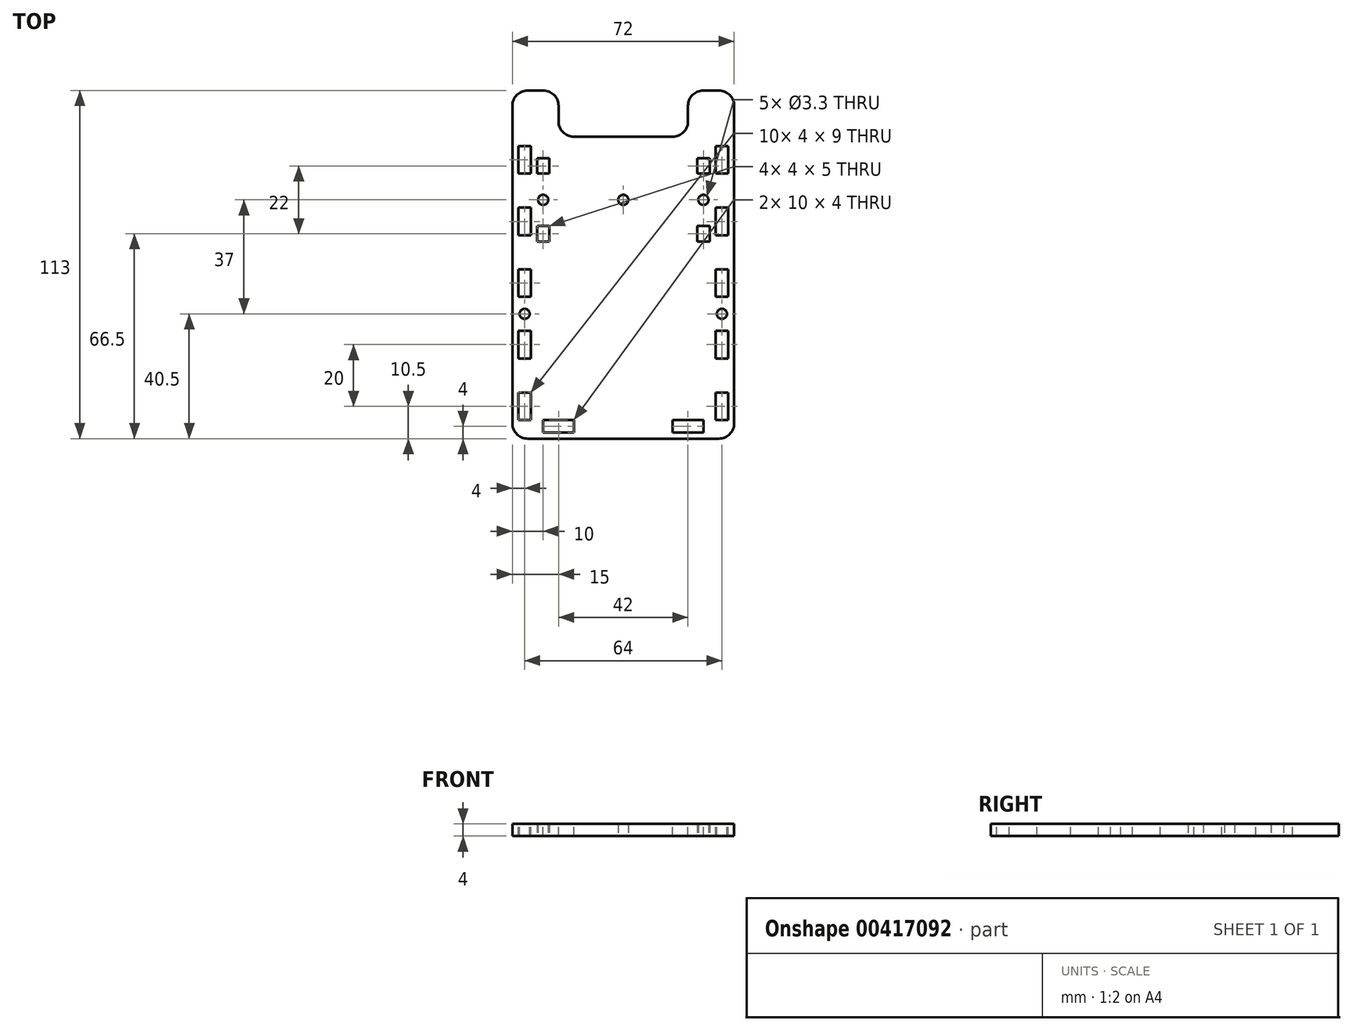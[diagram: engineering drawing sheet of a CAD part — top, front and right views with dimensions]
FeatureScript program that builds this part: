
annotation { "Feature Type Name" : "Feature", "Feature Type Description" : "" }
export const myFeature = defineFeature(function(context is Context, id is Id, definition is map)
    precondition{}
    {
        {
            var Q0;
            Q0=qCreatedBy(makeId("Top.planeOp"),FACE);
            var sketch = newSketch(context, id + "F0", { "sketchPlane" : qUnion([Q0])});
            skLineSegment(sketch, "E0.bottom", {"start": v(30, -17.5) * mm, "end": v(18.9, -17.5) * mm});
            skLineSegment(sketch, "E0.top", {"start": v(30, 17.5) * mm, "end": v(-30, 17.5) * mm});
            skLineSegment(sketch, "E0.left", {"start": v(30, -17.5) * mm, "end": v(30, 17.5) * mm});
            skLineSegment(sketch, "E0.right", {"start": v(-30, -17.5) * mm, "end": v(-30, 17.5) * mm});
            skPoint(sketch, "E0.middle", {"position": v(0, 0) * mm});
            skLineSegment(sketch, "E1.bottom", {"start": v(-24, 8.5) * mm, "end": v(-28, 8.5) * mm});
            skLineSegment(sketch, "E1.top", {"start": v(-24, 13.5) * mm, "end": v(-28, 13.5) * mm});
            skLineSegment(sketch, "E1.left", {"start": v(-24, 8.5) * mm, "end": v(-24, 13.5) * mm});
            skLineSegment(sketch, "E1.right", {"start": v(-28, 8.5) * mm, "end": v(-28, 13.5) * mm});
            skPoint(sketch, "E1.middle", {"position": v(-26, 11) * mm});
            skLineSegment(sketch, "E2.MirrorCS", {"start": v(-28, -8.5) * mm, "end": v(-28, -13.5) * mm});
            skLineSegment(sketch, "E3.MirrorCS", {"start": v(-24, -8.5) * mm, "end": v(-24, -13.5) * mm});
            skLineSegment(sketch, "E4.MirrorCS", {"start": v(-24, -8.5) * mm, "end": v(-28, -8.5) * mm});
            skLineSegment(sketch, "E5.MirrorCS", {"start": v(-24, -13.5) * mm, "end": v(-28, -13.5) * mm});
            skPoint(sketch, "E6.MirrorP", {"position": v(-26, -11) * mm});
            skPoint(sketch, "E7.MirrorP", {"position": v(26, 11) * mm});
            skPoint(sketch, "E8.MirrorP", {"position": v(26, -11) * mm});
            skLineSegment(sketch, "E9.MirrorCS", {"start": v(24, -13.5) * mm, "end": v(28, -13.5) * mm});
            skLineSegment(sketch, "E10.MirrorCS", {"start": v(24, -8.5) * mm, "end": v(28, -8.5) * mm});
            skLineSegment(sketch, "E11.MirrorCS", {"start": v(24, -8.5) * mm, "end": v(24, -13.5) * mm});
            skLineSegment(sketch, "E12.MirrorCS", {"start": v(24, 8.5) * mm, "end": v(28, 8.5) * mm});
            skLineSegment(sketch, "E13.MirrorCS", {"start": v(28, -8.5) * mm, "end": v(28, -13.5) * mm});
            skLineSegment(sketch, "E14.MirrorCS", {"start": v(28, 8.5) * mm, "end": v(28, 13.5) * mm});
            skLineSegment(sketch, "E15.MirrorCS", {"start": v(24, 8.5) * mm, "end": v(24, 13.5) * mm});
            skLineSegment(sketch, "E16.MirrorCS", {"start": v(24, 13.5) * mm, "end": v(28, 13.5) * mm});
            skPoint(sketch, "E17", {"position": v(-26, 0) * mm});
            skPoint(sketch, "E18.MirrorP", {"position": v(26, 0) * mm});
            skLineSegment(sketch, "E19", {"start": v(-18.9, -17.5) * mm, "end": v(-20, -14.5) * mm});
            skLineSegment(sketch, "E20", {"start": v(-20, -14.5) * mm, "end": v(-5, -14.5) * mm, "construction": true});
            skLineSegment(sketch, "E21", {"start": v(-5, -14.5) * mm, "end": v(-6.1, -17.5) * mm});
            skLineSegment(sketch, "E22.trimOffspring", {"start": v(-18.9, -17.5) * mm, "end": v(-30, -17.5) * mm});
            skLineSegment(sketch, "E23.MirrorCS", {"start": v(5, -14.5) * mm, "end": v(6.1, -17.5) * mm});
            skLineSegment(sketch, "E24.MirrorCS", {"start": v(18.9, -17.5) * mm, "end": v(20, -14.5) * mm});
            skLineSegment(sketch, "E25.MirrorCS", {"start": v(20, -14.5) * mm, "end": v(5, -14.5) * mm, "construction": true});
            skLineSegment(sketch, "E26.trimOffspring", {"start": v(6.1, -17.5) * mm, "end": v(-6.1, -17.5) * mm});
            skLineSegment(sketch, "E27", {"start": v(-18.9, -17.5) * mm, "end": v(-6.1, -17.5) * mm});
            skLineSegment(sketch, "E28", {"start": v(6.1, -17.5) * mm, "end": v(18.9, -17.5) * mm});
            skSolve(sketch);
        }
        {
            var Q0;
            Q0=makeQuery(id+"F0.imprint","IMPRINT",FACE,{"disambiguationData":[TD([[makeQuery(id+"F0.imprint","IMPRINT",EDGE,{"derivedFrom":sQuery(id+"F0.wireOp",EDGE,"E0.bottom")}),-1.0]])]});
            extrude(context, id + "F1", {"entities" : qUnion([Q0]), "depth" : 4 * mm});
        }
        {
            var Q0;
            Q0=sQuery(id+"F0.wireOp",VERTEX,"E17");
            var Q1;
            Q1=sQuery(id+"F0.wireOp",VERTEX,"E18.MirrorP");
            var Q2;
            Q2=makeQuery(id+"F1.opExtrude","SWEPT_BODY",BODY,{"disambiguationData":[OSD([sQuery(id+"F0.wireOp",EDGE,"E0.bottom"),sQuery(id+"F0.wireOp",EDGE,"E0.top"),sQuery(id+"F0.wireOp",EDGE,"E0.left"),sQuery(id+"F0.wireOp",EDGE,"E0.right"),sQuery(id+"F0.wireOp",EDGE,"E1.bottom"),sQuery(id+"F0.wireOp",EDGE,"E1.top"),sQuery(id+"F0.wireOp",EDGE,"E1.left"),sQuery(id+"F0.wireOp",EDGE,"E1.right"),sQuery(id+"F0.wireOp",EDGE,"E2.MirrorCS"),sQuery(id+"F0.wireOp",EDGE,"E3.MirrorCS"),sQuery(id+"F0.wireOp",EDGE,"E4.MirrorCS"),sQuery(id+"F0.wireOp",EDGE,"E5.MirrorCS"),sQuery(id+"F0.wireOp",EDGE,"E9.MirrorCS"),sQuery(id+"F0.wireOp",EDGE,"E10.MirrorCS"),sQuery(id+"F0.wireOp",EDGE,"E11.MirrorCS"),sQuery(id+"F0.wireOp",EDGE,"E12.MirrorCS"),sQuery(id+"F0.wireOp",EDGE,"E13.MirrorCS"),sQuery(id+"F0.wireOp",EDGE,"E14.MirrorCS"),sQuery(id+"F0.wireOp",EDGE,"E15.MirrorCS"),sQuery(id+"F0.wireOp",EDGE,"E16.MirrorCS"),sQuery(id+"F0.wireOp",EDGE,"sCp7zdMq-uB77-Oyxq-tNPJ-BeyvnlYmejad.bottom"),sQuery(id+"F0.wireOp",EDGE,"sCp7zdMq-uB77-Oyxq-tNPJ-BeyvnlYmejad.top"),sQuery(id+"F0.wireOp",EDGE,"sCp7zdMq-uB77-Oyxq-tNPJ-BeyvnlYmejad.left"),sQuery(id+"F0.wireOp",EDGE,"sCp7zdMq-uB77-Oyxq-tNPJ-BeyvnlYmejad.right")])]});
            hole(context, id + "F2", {"style" : HoleStyle.SIMPLE, "endStyle" : HoleEndStyle.THROUGH, "oppositeDirection" : true, "standardTappedOrClearance" : lookupTablePath({ "standard" : "ISO", "fit" : "Normal", "size" : "M3", "type" : "Clearance" }), "standardBlindInLast" : lookupTablePath({ "fit" : "Standard", "standard" : "ISO", "size" : "M3", "type" : "Clearance" }), "holeDiameter" : 3.3 * mm, "isTappedThrough" : true, "tappedDepth" : 12 * mm, "tapClearance" : 3, "startFromSketch" : true, "locations" : qUnion([Q0, Q1]), "scope" : qUnion([Q2])});
        }
        {
            var Q0;
            Q0=sQuery(id+"F0.wireOp",VERTEX,"E0.middle");
            var Q1;
            Q1=makeQuery(id+"F1.opExtrude","SWEPT_BODY",BODY,{"disambiguationData":[OSD([sQuery(id+"F0.wireOp",EDGE,"E0.bottom"),sQuery(id+"F0.wireOp",EDGE,"E0.top"),sQuery(id+"F0.wireOp",EDGE,"E0.left"),sQuery(id+"F0.wireOp",EDGE,"E0.right"),sQuery(id+"F0.wireOp",EDGE,"E1.bottom"),sQuery(id+"F0.wireOp",EDGE,"E1.top"),sQuery(id+"F0.wireOp",EDGE,"E1.left"),sQuery(id+"F0.wireOp",EDGE,"E1.right"),sQuery(id+"F0.wireOp",EDGE,"E2.MirrorCS"),sQuery(id+"F0.wireOp",EDGE,"E3.MirrorCS"),sQuery(id+"F0.wireOp",EDGE,"E4.MirrorCS"),sQuery(id+"F0.wireOp",EDGE,"E5.MirrorCS"),sQuery(id+"F0.wireOp",EDGE,"E9.MirrorCS"),sQuery(id+"F0.wireOp",EDGE,"E10.MirrorCS"),sQuery(id+"F0.wireOp",EDGE,"E11.MirrorCS"),sQuery(id+"F0.wireOp",EDGE,"E12.MirrorCS"),sQuery(id+"F0.wireOp",EDGE,"E13.MirrorCS"),sQuery(id+"F0.wireOp",EDGE,"E14.MirrorCS"),sQuery(id+"F0.wireOp",EDGE,"E15.MirrorCS"),sQuery(id+"F0.wireOp",EDGE,"E16.MirrorCS"),sQuery(id+"F0.wireOp",EDGE,"E19"),sQuery(id+"F0.wireOp",EDGE,"E20"),sQuery(id+"F0.wireOp",EDGE,"E21"),sQuery(id+"F0.wireOp",EDGE,"E22.trimOffspring"),sQuery(id+"F0.wireOp",EDGE,"E23.MirrorCS"),sQuery(id+"F0.wireOp",EDGE,"E24.MirrorCS"),sQuery(id+"F0.wireOp",EDGE,"E25.MirrorCS"),sQuery(id+"F0.wireOp",EDGE,"E26.trimOffspring")])]});
            hole(context, id + "F3", {"style" : HoleStyle.SIMPLE, "endStyle" : HoleEndStyle.THROUGH, "oppositeDirection" : true, "standardTappedOrClearance" : lookupTablePath({ "standard" : "ISO", "fit" : "Normal", "size" : "M3", "type" : "Clearance" }), "standardBlindInLast" : lookupTablePath({ "fit" : "Standard", "standard" : "ISO", "size" : "M3", "type" : "Clearance" }), "holeDiameter" : 3.3 * mm, "isTappedThrough" : true, "tappedDepth" : 12 * mm, "tapClearance" : 3, "startFromSketch" : true, "locations" : qUnion([Q0]), "scope" : qUnion([Q1])});
        }
        {
            var Q0;
            Q0=makeQuery(id+"F1.opExtrude","CAP_FACE",FACE,{"disambiguationData":[OSD([sQuery(id+"F0.wireOp",EDGE,"E0.bottom"),sQuery(id+"F0.wireOp",EDGE,"E0.top"),sQuery(id+"F0.wireOp",EDGE,"E0.left"),sQuery(id+"F0.wireOp",EDGE,"E0.right"),sQuery(id+"F0.wireOp",EDGE,"E1.bottom"),sQuery(id+"F0.wireOp",EDGE,"E1.top"),sQuery(id+"F0.wireOp",EDGE,"E1.left"),sQuery(id+"F0.wireOp",EDGE,"E1.right"),sQuery(id+"F0.wireOp",EDGE,"E2.MirrorCS"),sQuery(id+"F0.wireOp",EDGE,"E3.MirrorCS"),sQuery(id+"F0.wireOp",EDGE,"E4.MirrorCS"),sQuery(id+"F0.wireOp",EDGE,"E5.MirrorCS"),sQuery(id+"F0.wireOp",EDGE,"E9.MirrorCS"),sQuery(id+"F0.wireOp",EDGE,"E10.MirrorCS"),sQuery(id+"F0.wireOp",EDGE,"E11.MirrorCS"),sQuery(id+"F0.wireOp",EDGE,"E12.MirrorCS"),sQuery(id+"F0.wireOp",EDGE,"E13.MirrorCS"),sQuery(id+"F0.wireOp",EDGE,"E14.MirrorCS"),sQuery(id+"F0.wireOp",EDGE,"E15.MirrorCS"),sQuery(id+"F0.wireOp",EDGE,"E16.MirrorCS"),sQuery(id+"F0.wireOp",EDGE,"E22.trimOffspring"),sQuery(id+"F0.wireOp",EDGE,"E26.trimOffspring"),sQuery(id+"F0.wireOp",EDGE,"E27"),sQuery(id+"F0.wireOp",EDGE,"E28")])],"isStart":false});
            var sketch = newSketch(context, id + "F4", { "sketchPlane" : qUnion([Q0])});
            skLineSegment(sketch, "E29.bottom", {"start": v(36, 17.5) * mm, "end": v(-36, 17.5) * mm, "construction": true});
            skLineSegment(sketch, "E29.top", {"start": v(36, -77.5) * mm, "end": v(-36, -77.5) * mm});
            skLineSegment(sketch, "E29.left", {"start": v(36, 17.5) * mm, "end": v(36, -77.5) * mm});
            skLineSegment(sketch, "E29.right", {"start": v(-36, 17.5) * mm, "end": v(-36, -77.5) * mm});
            skPoint(sketch, "E29.middle", {"position": v(0, -30) * mm});
            skLineSegment(sketch, "E30", {"start": v(-36, 17.5) * mm, "end": v(-36, 35.5) * mm});
            skLineSegment(sketch, "E31", {"start": v(-36, 35.5) * mm, "end": v(-21, 35.5) * mm});
            skLineSegment(sketch, "E32", {"start": v(-21, 35.5) * mm, "end": v(-21, 20.5) * mm});
            skLineSegment(sketch, "E33", {"start": v(-21, 20.5) * mm, "end": v(0, 20.5) * mm});
            skLineSegment(sketch, "E34.MirrorCS", {"start": v(21, 20.5) * mm, "end": v(0, 20.5) * mm});
            skLineSegment(sketch, "E35.MirrorCS", {"start": v(21, 35.5) * mm, "end": v(21, 20.5) * mm});
            skLineSegment(sketch, "E36.MirrorCS", {"start": v(36, 35.5) * mm, "end": v(21, 35.5) * mm});
            skLineSegment(sketch, "E37.MirrorCS", {"start": v(36, 17.5) * mm, "end": v(36, 35.5) * mm});
            skLineSegment(sketch, "E38.bottom", {"start": v(-30, 17.5) * mm, "end": v(-34, 17.5) * mm});
            skLineSegment(sketch, "E38.top", {"start": v(-30, 8.5) * mm, "end": v(-34, 8.5) * mm});
            skLineSegment(sketch, "E38.left", {"start": v(-30, 17.5) * mm, "end": v(-30, 8.5) * mm});
            skLineSegment(sketch, "E38.right", {"start": v(-34, 17.5) * mm, "end": v(-34, 8.5) * mm});
            skLineSegment(sketch, "E39.0.1.0", {"start": v(-34, -2.5) * mm, "end": v(-34, -11.5) * mm});
            skLineSegment(sketch, "E39.0.1.1", {"start": v(-30, -11.5) * mm, "end": v(-34, -11.5) * mm});
            skLineSegment(sketch, "E39.0.1.2", {"start": v(-30, -2.5) * mm, "end": v(-30, -11.5) * mm});
            skLineSegment(sketch, "E39.0.1.3", {"start": v(-30, -2.5) * mm, "end": v(-34, -2.5) * mm});
            skLineSegment(sketch, "E39.0.2.0", {"start": v(-34, -22.5) * mm, "end": v(-34, -31.5) * mm});
            skLineSegment(sketch, "E39.0.2.1", {"start": v(-30, -31.5) * mm, "end": v(-34, -31.5) * mm});
            skLineSegment(sketch, "E39.0.2.2", {"start": v(-30, -22.5) * mm, "end": v(-30, -31.5) * mm});
            skLineSegment(sketch, "E39.0.2.3", {"start": v(-30, -22.5) * mm, "end": v(-34, -22.5) * mm});
            skLineSegment(sketch, "E39.0.3.0", {"start": v(-34, -42.5) * mm, "end": v(-34, -51.5) * mm});
            skLineSegment(sketch, "E39.0.3.1", {"start": v(-30, -51.5) * mm, "end": v(-34, -51.5) * mm});
            skLineSegment(sketch, "E39.0.3.2", {"start": v(-30, -42.5) * mm, "end": v(-30, -51.5) * mm});
            skLineSegment(sketch, "E39.0.3.3", {"start": v(-30, -42.5) * mm, "end": v(-34, -42.5) * mm});
            skLineSegment(sketch, "E39.0.4.0", {"start": v(-34, -62.5) * mm, "end": v(-34, -71.5) * mm});
            skLineSegment(sketch, "E39.0.4.1", {"start": v(-30, -71.5) * mm, "end": v(-34, -71.5) * mm});
            skLineSegment(sketch, "E39.0.4.2", {"start": v(-30, -62.5) * mm, "end": v(-30, -71.5) * mm});
            skLineSegment(sketch, "E39.0.4.3", {"start": v(-30, -62.5) * mm, "end": v(-34, -62.5) * mm});
            skLineSegment(sketch, "E39.direction1", {"start": v(-34, 8.5) * mm, "end": v(-8, 8.5) * mm, "construction": true});
            skLineSegment(sketch, "E39.direction2", {"start": v(-34, 8.5) * mm, "end": v(-34, -11.5) * mm, "construction": true});
            skLineSegment(sketch, "E40.MirrorCS", {"start": v(34, -2.5) * mm, "end": v(34, -11.5) * mm});
            skLineSegment(sketch, "E41.MirrorCS", {"start": v(30, 17.5) * mm, "end": v(34, 17.5) * mm});
            skLineSegment(sketch, "E42.MirrorCS", {"start": v(30, 8.5) * mm, "end": v(34, 8.5) * mm});
            skLineSegment(sketch, "E43.MirrorCS", {"start": v(30, -42.5) * mm, "end": v(30, -51.5) * mm});
            skLineSegment(sketch, "E44.MirrorCS", {"start": v(30, -2.5) * mm, "end": v(34, -2.5) * mm});
            skLineSegment(sketch, "E45.MirrorCS", {"start": v(30, -51.5) * mm, "end": v(34, -51.5) * mm});
            skLineSegment(sketch, "E46.MirrorCS", {"start": v(30, -2.5) * mm, "end": v(30, -11.5) * mm});
            skLineSegment(sketch, "E47.MirrorCS", {"start": v(34, -42.5) * mm, "end": v(34, -51.5) * mm});
            skLineSegment(sketch, "E48.MirrorCS", {"start": v(30, -11.5) * mm, "end": v(34, -11.5) * mm});
            skLineSegment(sketch, "E49.MirrorCS", {"start": v(34, 8.5) * mm, "end": v(34, -11.5) * mm, "construction": true});
            skLineSegment(sketch, "E50.MirrorCS", {"start": v(30, -22.5) * mm, "end": v(34, -22.5) * mm});
            skLineSegment(sketch, "E51.MirrorCS", {"start": v(34, 8.5) * mm, "end": v(8, 8.5) * mm, "construction": true});
            skLineSegment(sketch, "E52.MirrorCS", {"start": v(-36, 17.5) * mm, "end": v(36, 17.5) * mm, "construction": true});
            skLineSegment(sketch, "E53.MirrorCS", {"start": v(30, -31.5) * mm, "end": v(34, -31.5) * mm});
            skLineSegment(sketch, "E54.MirrorCS", {"start": v(30, 17.5) * mm, "end": v(30, 8.5) * mm});
            skLineSegment(sketch, "E55.MirrorCS", {"start": v(30, -62.5) * mm, "end": v(30, -71.5) * mm});
            skLineSegment(sketch, "E56.MirrorCS", {"start": v(30, -62.5) * mm, "end": v(34, -62.5) * mm});
            skLineSegment(sketch, "E57.MirrorCS", {"start": v(34, 17.5) * mm, "end": v(34, 8.5) * mm});
            skLineSegment(sketch, "E58.MirrorCS", {"start": v(30, -42.5) * mm, "end": v(34, -42.5) * mm});
            skLineSegment(sketch, "E59.MirrorCS", {"start": v(30, -71.5) * mm, "end": v(34, -71.5) * mm});
            skLineSegment(sketch, "E60.MirrorCS", {"start": v(30, -22.5) * mm, "end": v(30, -31.5) * mm});
            skLineSegment(sketch, "E61.MirrorCS", {"start": v(34, -22.5) * mm, "end": v(34, -31.5) * mm});
            skLineSegment(sketch, "E62.MirrorCS", {"start": v(34, -62.5) * mm, "end": v(34, -71.5) * mm});
            skLineSegment(sketch, "E63.bottom", {"start": v(-26, -71.5) * mm, "end": v(-16, -71.5) * mm});
            skLineSegment(sketch, "E63.top", {"start": v(-26, -75.5) * mm, "end": v(-16, -75.5) * mm});
            skLineSegment(sketch, "E63.left", {"start": v(-26, -71.5) * mm, "end": v(-26, -75.5) * mm});
            skLineSegment(sketch, "E63.right", {"start": v(-16, -71.5) * mm, "end": v(-16, -75.5) * mm});
            skLineSegment(sketch, "E64.MirrorCS", {"start": v(26, -75.5) * mm, "end": v(16, -75.5) * mm});
            skLineSegment(sketch, "E65.MirrorCS", {"start": v(26, -71.5) * mm, "end": v(26, -75.5) * mm});
            skLineSegment(sketch, "E66.MirrorCS", {"start": v(16, -71.5) * mm, "end": v(16, -75.5) * mm});
            skLineSegment(sketch, "E67.MirrorCS", {"start": v(26, -71.5) * mm, "end": v(16, -71.5) * mm});
            skLineSegment(sketch, "E68", {"start": v(-32, -31.5) * mm, "end": v(-32, -42.5) * mm, "construction": true});
            skPoint(sketch, "E69", {"position": v(-32, -37) * mm});
            skLineSegment(sketch, "E70", {"start": v(32, -31.5) * mm, "end": v(32, -42.5) * mm, "construction": true});
            skPoint(sketch, "E71", {"position": v(32, -37) * mm});
            skSolve(sketch);
        }
        {
            var Q0;
            Q0=makeQuery(id+"F4.imprint","IMPRINT",FACE,{"disambiguationData":[TD([[makeQuery(id+"F4.imprint","IMPRINT",EDGE,{"derivedFrom":sQuery(id+"F4.wireOp",EDGE,"E29.top")}),-1.0]])]});
            extrude(context, id + "F5", {"entities" : qUnion([Q0]), "operationType" : NewBodyOperationType.ADD, "oppositeDirection" : true, "depth" : 4 * mm});
        }
        {
            var Q0;
            Q0=sQuery(id+"F4.wireOp",VERTEX,"E69");
            var Q1;
            Q1=sQuery(id+"F4.wireOp",VERTEX,"E71");
            var Q2;
            Q2=makeQuery(id+"F1.opExtrude","SWEPT_BODY",BODY,{"disambiguationData":[OSD([sQuery(id+"F0.wireOp",EDGE,"E0.bottom"),sQuery(id+"F0.wireOp",EDGE,"E0.top"),sQuery(id+"F0.wireOp",EDGE,"E0.left"),sQuery(id+"F0.wireOp",EDGE,"E0.right"),sQuery(id+"F0.wireOp",EDGE,"E1.bottom"),sQuery(id+"F0.wireOp",EDGE,"E1.top"),sQuery(id+"F0.wireOp",EDGE,"E1.left"),sQuery(id+"F0.wireOp",EDGE,"E1.right"),sQuery(id+"F0.wireOp",EDGE,"E2.MirrorCS"),sQuery(id+"F0.wireOp",EDGE,"E3.MirrorCS"),sQuery(id+"F0.wireOp",EDGE,"E4.MirrorCS"),sQuery(id+"F0.wireOp",EDGE,"E5.MirrorCS"),sQuery(id+"F0.wireOp",EDGE,"E9.MirrorCS"),sQuery(id+"F0.wireOp",EDGE,"E10.MirrorCS"),sQuery(id+"F0.wireOp",EDGE,"E11.MirrorCS"),sQuery(id+"F0.wireOp",EDGE,"E12.MirrorCS"),sQuery(id+"F0.wireOp",EDGE,"E13.MirrorCS"),sQuery(id+"F0.wireOp",EDGE,"E14.MirrorCS"),sQuery(id+"F0.wireOp",EDGE,"E15.MirrorCS"),sQuery(id+"F0.wireOp",EDGE,"E16.MirrorCS"),sQuery(id+"F0.wireOp",EDGE,"E22.trimOffspring"),sQuery(id+"F0.wireOp",EDGE,"E26.trimOffspring"),sQuery(id+"F0.wireOp",EDGE,"E27"),sQuery(id+"F0.wireOp",EDGE,"E28")])]});
            hole(context, id + "F6", {"style" : HoleStyle.SIMPLE, "endStyle" : HoleEndStyle.THROUGH, "standardTappedOrClearance" : lookupTablePath({ "standard" : "ISO", "fit" : "Normal", "size" : "M3", "type" : "Clearance" }), "standardBlindInLast" : lookupTablePath({ "fit" : "Standard", "standard" : "ISO", "size" : "M3", "type" : "Clearance" }), "holeDiameter" : 3.3 * mm, "isTappedThrough" : true, "tappedDepth" : 12 * mm, "tapClearance" : 3, "startFromSketch" : true, "locations" : qUnion([Q0, Q1]), "scope" : qUnion([Q2])});
        }
        {
            var Q0;
            Q0=makeQuery(id+"F5.opExtrude","SWEPT_EDGE",EDGE,{"disambiguationData":[OSD([sQuery(id+"F4.wireOp",EDGE,"E29.top"),sQuery(id+"F4.wireOp",EDGE,"E29.right")])]});
            var Q1;
            Q1=makeQuery(id+"F5.opExtrude","SWEPT_EDGE",EDGE,{"disambiguationData":[OSD([sQuery(id+"F4.wireOp",EDGE,"E29.top"),sQuery(id+"F4.wireOp",EDGE,"E29.left")])]});
            var Q2;
            Q2=makeQuery(id+"F5.opExtrude","SWEPT_EDGE",EDGE,{"disambiguationData":[OSD([sQuery(id+"F4.wireOp",EDGE,"E32"),sQuery(id+"F4.wireOp",EDGE,"E33")])]});
            var Q3;
            Q3=makeQuery(id+"F5.opExtrude","SWEPT_EDGE",EDGE,{"disambiguationData":[OSD([sQuery(id+"F4.wireOp",EDGE,"E31"),sQuery(id+"F4.wireOp",EDGE,"E32")])]});
            var Q4;
            Q4=makeQuery(id+"F5.opExtrude","SWEPT_EDGE",EDGE,{"disambiguationData":[OSD([sQuery(id+"F4.wireOp",EDGE,"E30"),sQuery(id+"F4.wireOp",EDGE,"E31")])]});
            var Q5;
            Q5=makeQuery(id+"F5.opExtrude","SWEPT_EDGE",EDGE,{"disambiguationData":[OSD([sQuery(id+"F4.wireOp",EDGE,"E35.MirrorCS"),sQuery(id+"F4.wireOp",EDGE,"E36.MirrorCS")])]});
            var Q6;
            Q6=makeQuery(id+"F5.opExtrude","SWEPT_EDGE",EDGE,{"disambiguationData":[OSD([sQuery(id+"F4.wireOp",EDGE,"E34.MirrorCS"),sQuery(id+"F4.wireOp",EDGE,"E35.MirrorCS")])]});
            var Q7;
            Q7=makeQuery(id+"F5.opExtrude","SWEPT_EDGE",EDGE,{"disambiguationData":[OSD([sQuery(id+"F4.wireOp",EDGE,"E36.MirrorCS"),sQuery(id+"F4.wireOp",EDGE,"E37.MirrorCS")])]});
            fillet(context, id + "F7", {"entities" : qUnion([Q0, Q1, Q2, Q3, Q4, Q5, Q6, Q7]), "radius" : 5 * mm, "tangentPropagation" : true, "allowEdgeOverflow" : false});
        }
    });
